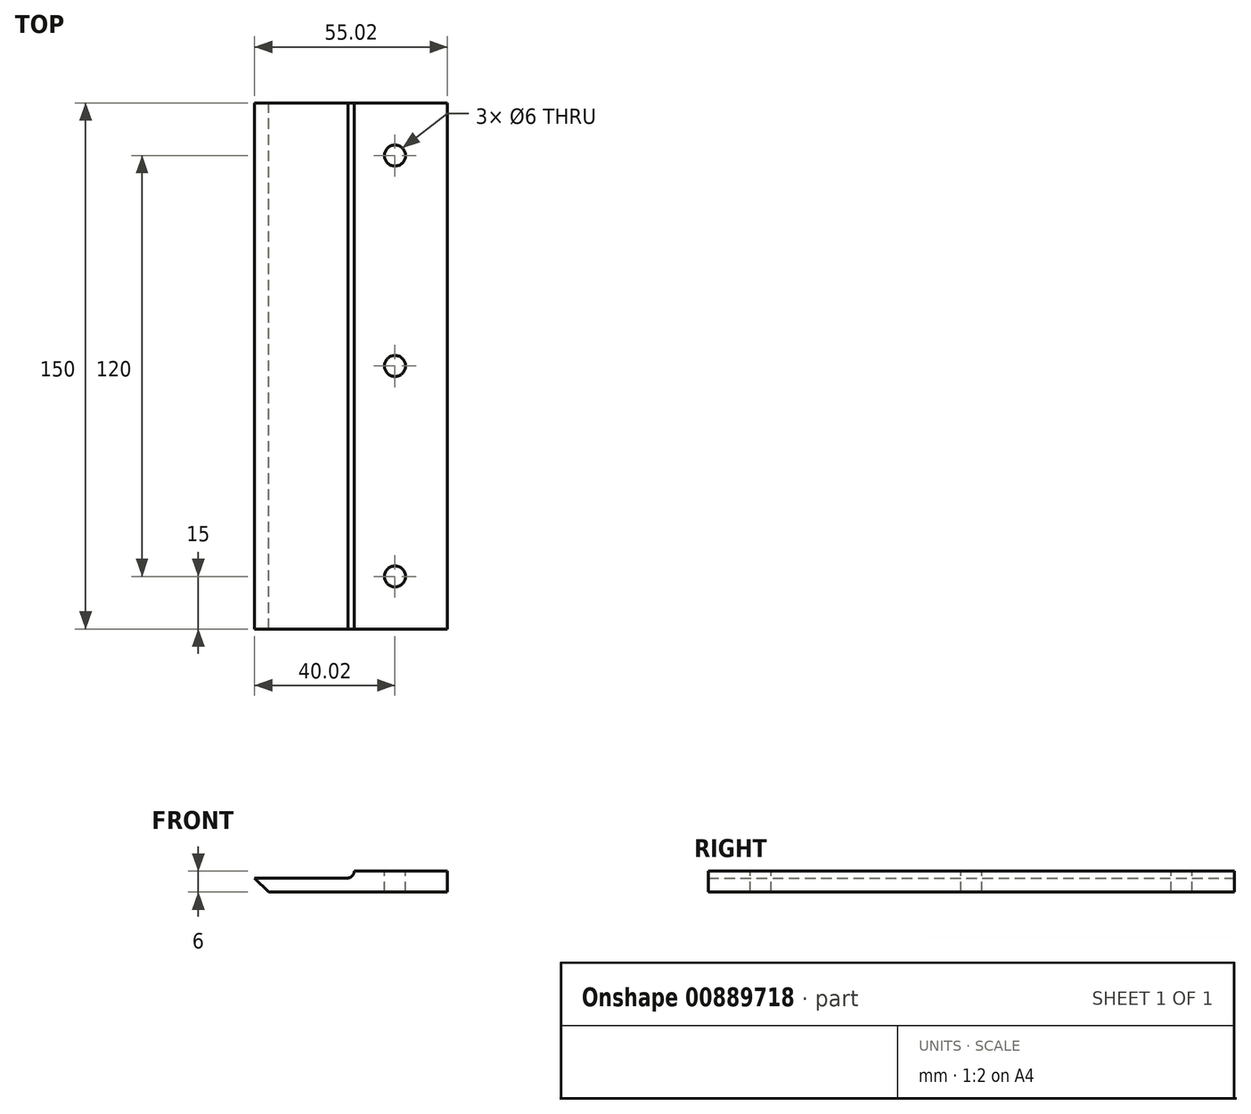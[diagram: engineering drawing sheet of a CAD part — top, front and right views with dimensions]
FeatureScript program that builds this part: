
annotation { "Feature Type Name" : "Feature", "Feature Type Description" : "" }
export const myFeature = defineFeature(function(context is Context, id is Id, definition is map)
    precondition{}
    {
        {
            var Q0;
            Q0=qCreatedBy(makeId("Front.planeOp"),FACE);
            var sketch = newSketch(context, id + "F0", { "sketchPlane" : qUnion([Q0])});
            skLineSegment(sketch, "E0.bottom", {"start": v(0, 0) * mm, "end": v(-26.6, 0) * mm});
            skLineSegment(sketch, "E0.top", {"start": v(0, -6) * mm, "end": v(-51, -6) * mm});
            skLineSegment(sketch, "E0.left", {"start": v(0, 0) * mm, "end": v(0, -6) * mm});
            skLineSegment(sketch, "E1", {"start": v(-55.02, -1.98) * mm, "end": v(-51, -6) * mm});
            skArc(sketch, "E2", {"start": v(-28.34, -1.98) * mm, "mid": v(-27.1, -1.32) * mm, "end": v(-26.6, 0) * mm});
            skPoint(sketch, "E3.end.orphan", {"position": v(-54, -3) * mm});
            skPoint(sketch, "E4.center.orphan", {"position": v(-51, 0) * mm});
            skPoint(sketch, "E5.center.orphan", {"position": v(-46, 0) * mm});
            skPoint(sketch, "E6.orphan", {"position": v(-57, 0) * mm});
            skLineSegment(sketch, "E7", {"start": v(-28.34, -1.98) * mm, "end": v(-55.02, -1.98) * mm});
            skSolve(sketch);
        }
        {
            var Q0;
            Q0 = qSketchRegion(id + "F0", true);
            extrude(context, id + "F1", {"entities" : qUnion([Q0]), "depth" : 150 * mm, "offsetDistance" : 25 * mm});
        }
        {
            var Q0;
            Q0=makeQuery(id+"F1.opExtrude","SWEPT_FACE",FACE,{"disambiguationData":[OSD([sQuery(id+"F0.wireOp",EDGE,"E0.bottom")])]});
            cPlane(context, id + "F2", {"entities" : qUnion([Q0]), "cplaneType" : CPlaneType.OFFSET, "offset" : 0 * mm, "width" : 150 * mm, "height" : 150 * mm});
        }
        {
            var Q0;
            Q0=qCreatedBy(id+"F2.planeOp",FACE);
            var sketch = newSketch(context, id + "F3", { "sketchPlane" : qUnion([Q0])});
            skLineSegment(sketch, "E8", {"start": v(-46.77, -15) * mm, "end": v(25.67, -15) * mm, "construction": true});
            skLineSegment(sketch, "E9", {"start": v(-45.44, -135) * mm, "end": v(21.23, -135) * mm, "construction": true});
            skLineSegment(sketch, "E10", {"start": v(-15, -9.34) * mm, "end": v(-15, -136.9) * mm, "construction": true});
            skLineSegment(sketch, "E11", {"start": v(-58.23, -75) * mm, "end": v(40.03, -75) * mm, "construction": true});
            skCircle(sketch, "E12", {"center": v(-15, -15) * mm, "radius": 3 * mm});
            skCircle(sketch, "E13", {"center": v(-15, -135) * mm, "radius": 3 * mm});
            skCircle(sketch, "E14", {"center": v(-15, -75) * mm, "radius": 3 * mm});
            skSolve(sketch);
        }
        {
            var Q0;
            Q0 = qSketchRegion(id + "F3", true);
            extrude(context, id + "F4", {"entities" : qUnion([Q0]), "operationType" : NewBodyOperationType.REMOVE, "oppositeDirection" : true, "depth" : 25 * mm, "offsetDistance" : 25 * mm});
        }
    });
